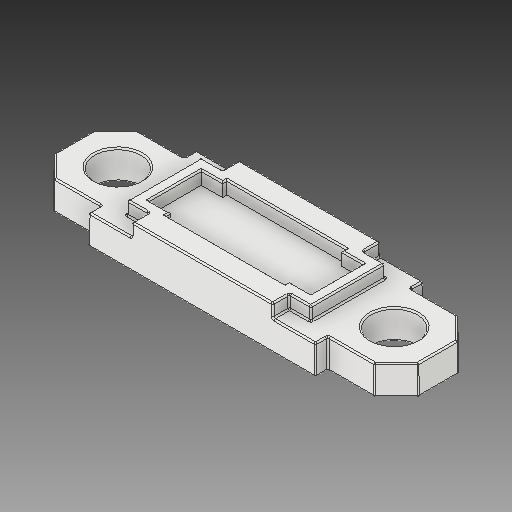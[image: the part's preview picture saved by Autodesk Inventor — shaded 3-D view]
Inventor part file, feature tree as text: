
AUTODESK INVENTOR PART (.ipt)
format: ipt  version: 2019 (Build 230136000, 136)  size: 349,184 bytes
history: native  units: in
note: dims shown in document units (in); Inventor stores cm internally (conversion verified against a paired STEP export)
features: fillet x1
ambient origin geometry x8: Origin, YZ Plane, XZ Plane, XY Plane, X Axis, Y Axis, Z Axis, Center Point
bodies: Solid1 (feature_tree)
feature tree (1):
  fillet  "Fillet1"  [1 undecoded]
note: 1 required parameter value undecoded (feature->parameter linkage not recoverable at this tier; creation-order binding heuristic only, values carry confidence <= 0.55)
